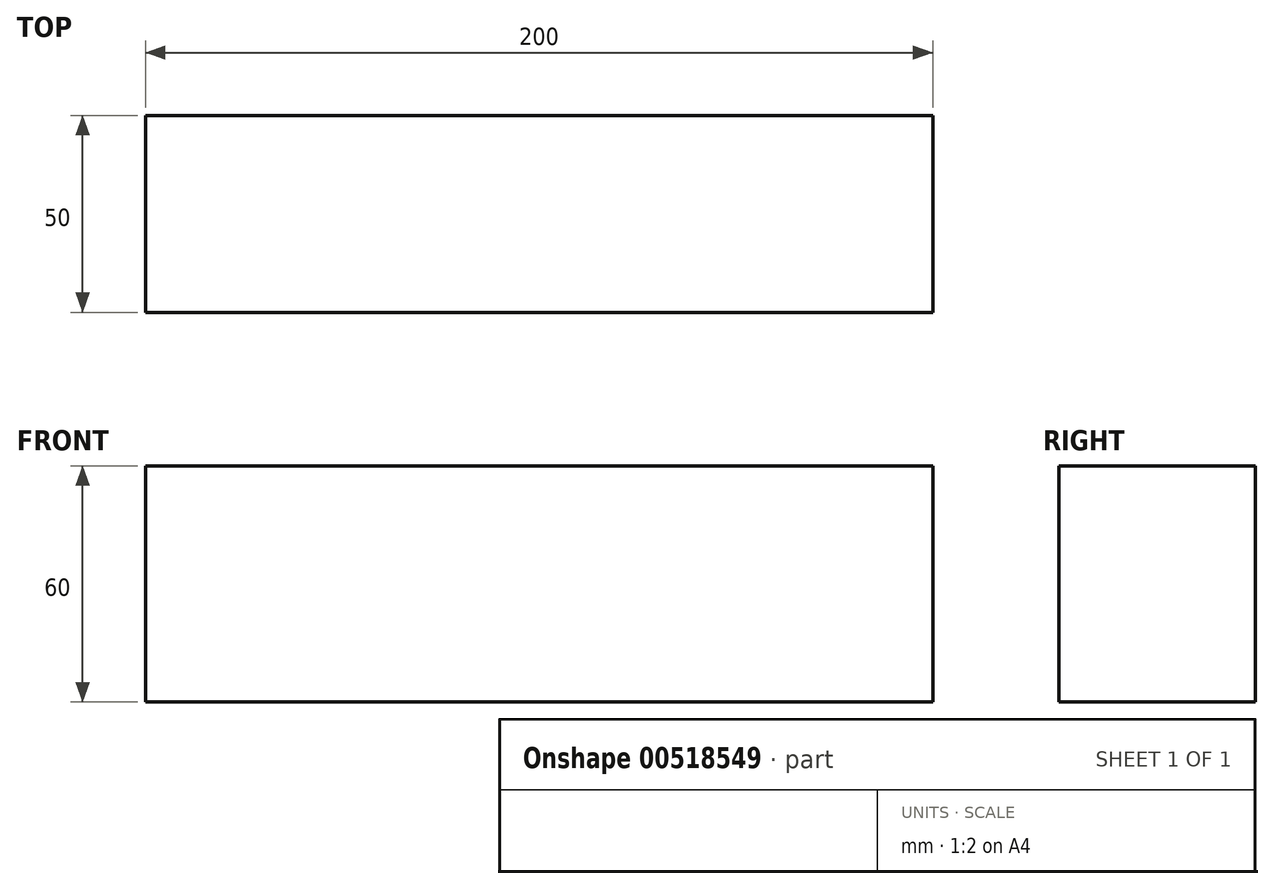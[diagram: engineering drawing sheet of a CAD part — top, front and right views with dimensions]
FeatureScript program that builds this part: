
annotation { "Feature Type Name" : "Feature", "Feature Type Description" : "" }
export const myFeature = defineFeature(function(context is Context, id is Id, definition is map)
    precondition{}
    {
        {
            var Q0;
            Q0=qCreatedBy(makeId("Top.planeOp"),FACE);
            var sketch = newSketch(context, id + "F0", { "sketchPlane" : qUnion([Q0])});
            skLineSegment(sketch, "E0.bottom", {"start": v(0, 0) * mm, "end": v(200, 0) * mm});
            skLineSegment(sketch, "E0.top", {"start": v(0, 50) * mm, "end": v(200, 50) * mm});
            skLineSegment(sketch, "E0.left", {"start": v(0, 0) * mm, "end": v(0, 50) * mm});
            skLineSegment(sketch, "E0.right", {"start": v(200, 0) * mm, "end": v(200, 50) * mm});
            skSolve(sketch);
        }
        {
            var Q0;
            Q0 = qSketchRegion(id + "F0", true);
            extrude(context, id + "F1", {"entities" : qUnion([Q0]), "depth" : 60 * mm, "offsetDistance" : 25 * mm});
        }
    });
